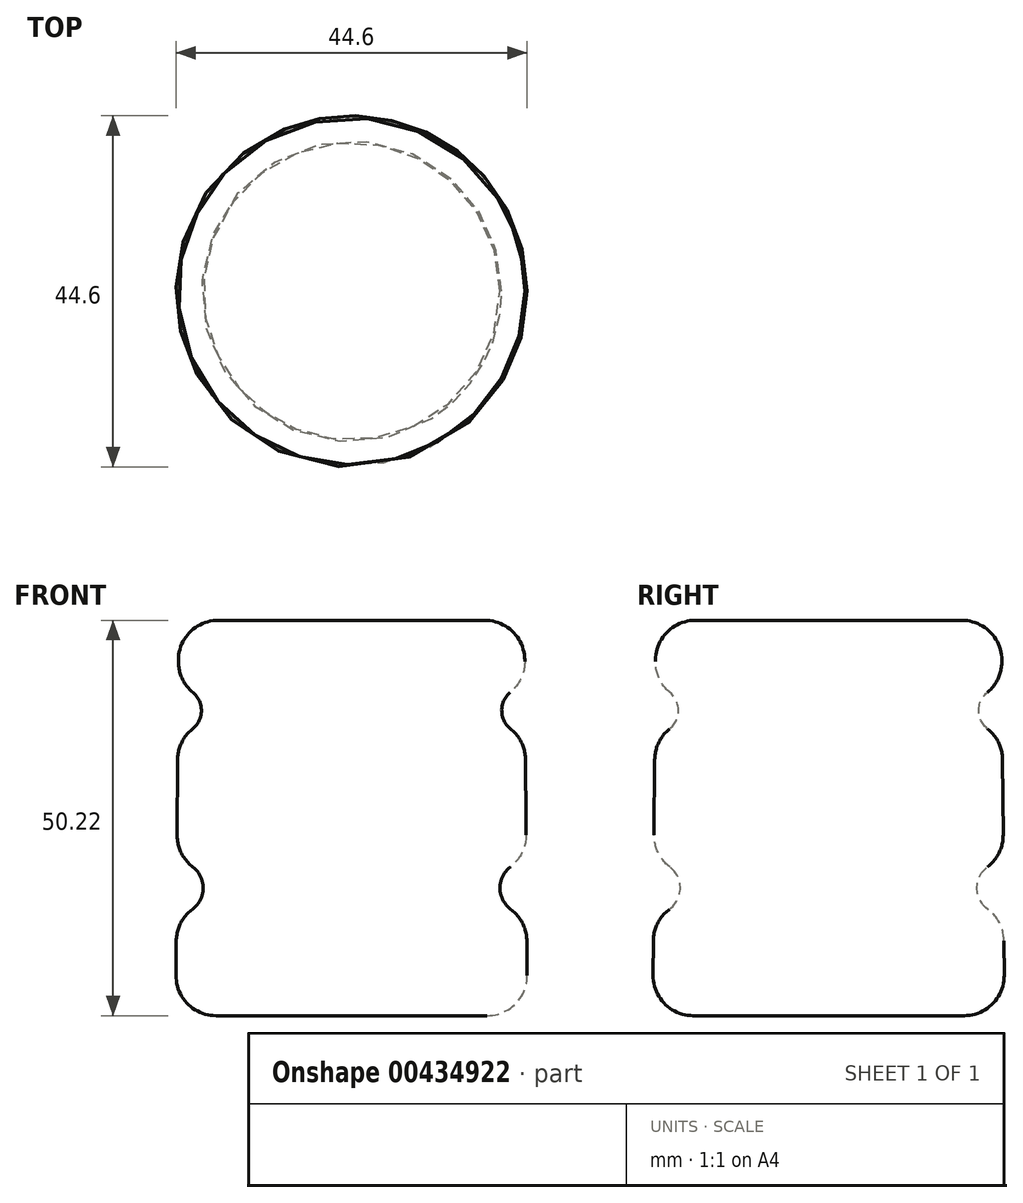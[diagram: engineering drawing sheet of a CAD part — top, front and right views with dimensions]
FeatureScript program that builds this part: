
annotation { "Feature Type Name" : "Feature", "Feature Type Description" : "" }
export const myFeature = defineFeature(function(context is Context, id is Id, definition is map)
    precondition{}
    {
        {
            var Q0;
            Q0=qCreatedBy(makeId("Front.planeOp"),FACE);
            var sketch = newSketch(context, id + "F0", { "sketchPlane" : qUnion([Q0])});
            skLineSegment(sketch, "E0", {"start": v(-63.78, 59) * mm, "end": v(-63.78, 8.78) * mm});
            skLineSegment(sketch, "E1", {"start": v(-63.78, 8.78) * mm, "end": v(-41.44, 8.78) * mm});
            skLineSegment(sketch, "E2", {"start": v(-63.78, 59) * mm, "end": v(-41.82, 59) * mm});
            skLineSegment(sketch, "E3", {"start": v(-41.82, 59) * mm, "end": v(-41.75, 50.52) * mm});
            skArc(sketch, "E4", {"start": v(-41.75, 50.52) * mm, "mid": v(-44.7, 47.52) * mm, "end": v(-41.7, 44.57) * mm});
            skArc(sketch, "E5", {"start": v(-41.59, 28.38) * mm, "mid": v(-44.93, 24.98) * mm, "end": v(-41.53, 21.64) * mm});
            skLineSegment(sketch, "E6.trimOffspring", {"start": v(-41.7, 44.57) * mm, "end": v(-41.59, 28.38) * mm});
            skLineSegment(sketch, "E7.trimOffspring", {"start": v(-41.53, 21.64) * mm, "end": v(-41.44, 8.78) * mm});
            skSolve(sketch);
        }
        {
            var Q0;
            Q0=makeQuery(id+"F0.imprint","IMPRINT",FACE,{"disambiguationData":[TD([[makeQuery(id+"F0.imprint","IMPRINT",EDGE,{"derivedFrom":sQuery(id+"F0.wireOp",EDGE,"E0")}),1.0]])]});
            var Q1;
            Q1=sQuery(id+"F0.wireOp",EDGE,"E0");
            revolve(context, id + "F1", {"entities" : qUnion([Q0]), "axis" : qUnion([Q1]), "revolveType" : RevolveType.FULL});
        }
        {
            var Q0;
            Q0=makeQuery(id+"F1.opRevolve","SWEPT_EDGE",EDGE,{"disambiguationData":[OSD([sQuery(id+"F0.wireOp",EDGE,"E2"),sQuery(id+"F0.wireOp",EDGE,"E3")])]});
            var Q1;
            Q1=makeQuery(id+"F1.opRevolve","SWEPT_EDGE",EDGE,{"disambiguationData":[OSD([sQuery(id+"F0.wireOp",EDGE,"E3"),sQuery(id+"F0.wireOp",EDGE,"E4")])]});
            var Q2;
            Q2=makeQuery(id+"F1.opRevolve","SWEPT_EDGE",EDGE,{"disambiguationData":[OSD([sQuery(id+"F0.wireOp",EDGE,"E4"),sQuery(id+"F0.wireOp",EDGE,"E6.trimOffspring")])]});
            var Q3;
            Q3=makeQuery(id+"F1.opRevolve","SWEPT_EDGE",EDGE,{"disambiguationData":[OSD([sQuery(id+"F0.wireOp",EDGE,"E5"),sQuery(id+"F0.wireOp",EDGE,"E6.trimOffspring")])]});
            var Q4;
            Q4=makeQuery(id+"F1.opRevolve","SWEPT_FACE",FACE,{"disambiguationData":[OSD([sQuery(id+"F0.wireOp",EDGE,"E5")])]});
            var Q5;
            Q5=makeQuery(id+"F1.opRevolve","SWEPT_EDGE",EDGE,{"disambiguationData":[OSD([sQuery(id+"F0.wireOp",EDGE,"E1"),sQuery(id+"F0.wireOp",EDGE,"E7.trimOffspring")])]});
            fillet(context, id + "F2", {"entities" : qUnion([Q0, Q1, Q2, Q3, Q4, Q5]), "radius" : 5.08 * mm, "tangentPropagation" : true, "allowEdgeOverflow" : false});
        }
    });
